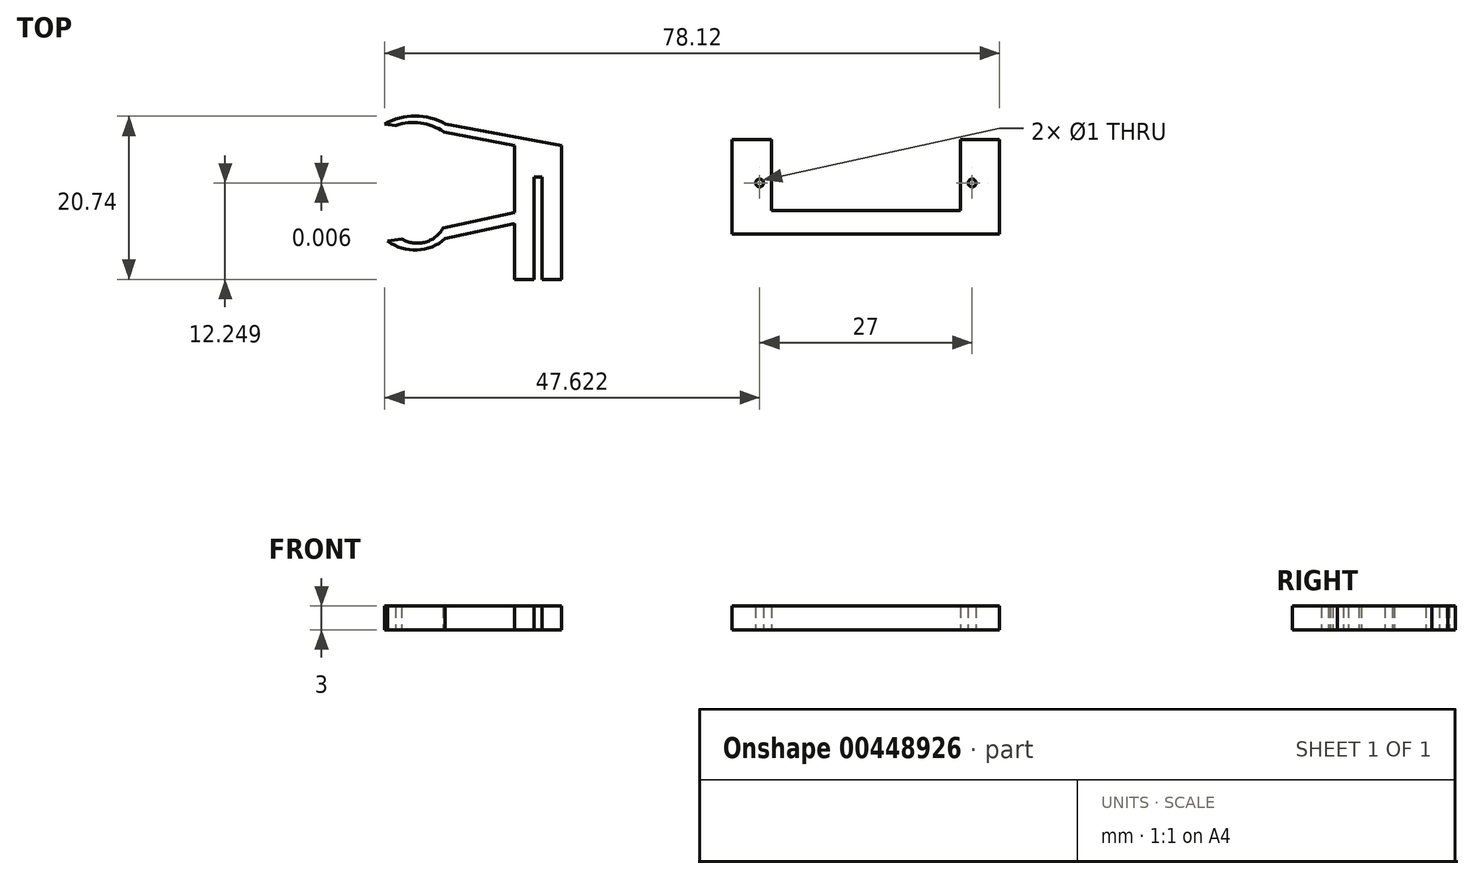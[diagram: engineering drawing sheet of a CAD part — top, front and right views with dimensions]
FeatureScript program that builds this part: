
annotation { "Feature Type Name" : "Feature", "Feature Type Description" : "" }
export const myFeature = defineFeature(function(context is Context, id is Id, definition is map)
    precondition{}
    {
        {
            var Q0;
            Q0=qCreatedBy(makeId("Top.planeOp"),FACE);
            var sketch = newSketch(context, id + "F0", { "sketchPlane" : qUnion([Q0])});
            skLineSegment(sketch, "E0.bottom", {"start": v(14.51, -20.17) * mm, "end": v(48.51, -20.17) * mm});
            skLineSegment(sketch, "E0.top", {"start": v(14.51, -23.17) * mm, "end": v(48.51, -23.17) * mm});
            skLineSegment(sketch, "E0.left", {"start": v(14.51, -20.17) * mm, "end": v(14.51, -23.17) * mm});
            skLineSegment(sketch, "E0.right", {"start": v(48.51, -20.17) * mm, "end": v(48.51, -23.17) * mm});
            skLineSegment(sketch, "E1.bottom", {"start": v(14.51, -23.17) * mm, "end": v(19.51, -23.17) * mm});
            skLineSegment(sketch, "E1.top", {"start": v(14.51, -11.17) * mm, "end": v(19.51, -11.17) * mm});
            skLineSegment(sketch, "E1.left", {"start": v(14.51, -23.17) * mm, "end": v(14.51, -11.17) * mm});
            skLineSegment(sketch, "E1.right", {"start": v(19.51, -23.17) * mm, "end": v(19.51, -11.17) * mm});
            skLineSegment(sketch, "E2.bottom", {"start": v(48.51, -23.17) * mm, "end": v(43.51, -23.17) * mm});
            skLineSegment(sketch, "E3", {"start": v(43.51, -23.17) * mm, "end": v(43.51, -11.18) * mm});
            skLineSegment(sketch, "E4", {"start": v(48.51, -23.17) * mm, "end": v(48.51, -11.17) * mm});
            skLineSegment(sketch, "E5", {"start": v(48.51, -11.17) * mm, "end": v(43.51, -11.18) * mm});
            skCircle(sketch, "E6", {"center": v(45.01, -16.68) * mm, "radius": 0.5 * mm});
            skCircle(sketch, "E7", {"center": v(18.01, -16.67) * mm, "radius": 0.5 * mm});
            skSolve(sketch);
        }
        {
            var Q0;
            {var subQ5=sQuery(id+"F0.wireOp",EDGE,"E1.bottom");Q0=makeQuery(id+"F0.imprint","IMPRINT",FACE,{"disambiguationData":[TD([[makeQuery(id+"F0.imprint","IMPRINT",EDGE,{"derivedFrom":subQ5}),1.0]])]});}
            var Q1;
            {var subQ1=sQuery(id+"F0.wireOp",EDGE,"E1.top");Q1=makeQuery(id+"F0.imprint","IMPRINT",FACE,{"disambiguationData":[TD([[makeQuery(id+"F0.imprint","IMPRINT",EDGE,{"derivedFrom":subQ1}),-1.0]])]});}
            var Q2;
            {var subQ5=sQuery(id+"F0.wireOp",EDGE,"E2.bottom");Q2=makeQuery(id+"F0.imprint","IMPRINT",FACE,{"disambiguationData":[TD([[makeQuery(id+"F0.imprint","IMPRINT",EDGE,{"derivedFrom":subQ5}),-1.0]])]});}
            var Q3;
            {var subQ0=sQuery(id+"F0.wireOp",EDGE,"E5");Q3=makeQuery(id+"F0.imprint","IMPRINT",FACE,{"disambiguationData":[TD([[makeQuery(id+"F0.imprint","IMPRINT",EDGE,{"derivedFrom":subQ0}),1.0]])]});}
            var Q4;
            {var subQ5=sQuery(id+"F0.wireOp",EDGE,"E0.top");Q4=makeQuery(id+"F0.imprint","IMPRINT",FACE,{"disambiguationData":[TD([[makeQuery(id+"F0.imprint","IMPRINT",EDGE,{"derivedFrom":subQ5}),1.0]])]});}
            extrude(context, id + "F1", {"entities" : qUnion([Q0, Q1, Q2, Q3, Q4]), "depth" : 3 * mm});
        }
        {
            var Q0;
            Q0=qCreatedBy(makeId("Top.planeOp"),FACE);
            var sketch = newSketch(context, id + "F2", { "sketchPlane" : qUnion([Q0])});
            skLineSegment(sketch, "E8.bottom", {"start": v(-13.12, -11.93) * mm, "end": v(-7.12, -11.93) * mm});
            skLineSegment(sketch, "E8.top", {"start": v(-13.12, -28.93) * mm, "end": v(-7.12, -28.93) * mm});
            skLineSegment(sketch, "E8.left", {"start": v(-13.12, -11.93) * mm, "end": v(-13.12, -28.93) * mm});
            skLineSegment(sketch, "E8.right", {"start": v(-7.12, -11.93) * mm, "end": v(-7.12, -28.93) * mm});
            skLineSegment(sketch, "E9.bottom", {"start": v(-10.62, -15.93) * mm, "end": v(-9.62, -15.93) * mm});
            skLineSegment(sketch, "E9.top", {"start": v(-10.62, -28.93) * mm, "end": v(-9.62, -28.93) * mm});
            skLineSegment(sketch, "E9.left", {"start": v(-10.62, -15.93) * mm, "end": v(-10.62, -28.93) * mm});
            skLineSegment(sketch, "E9.right", {"start": v(-9.62, -15.93) * mm, "end": v(-9.62, -28.93) * mm});
            skLineSegment(sketch, "E10.bottom", {"start": v(-13.12, -27.9) * mm, "end": v(-12.42, -27.9) * mm});
            skLineSegment(sketch, "E10.top", {"start": v(-13.12, -24.9) * mm, "end": v(-12.42, -24.9) * mm});
            skLineSegment(sketch, "E10.left", {"start": v(-13.12, -27.9) * mm, "end": v(-13.12, -24.9) * mm});
            skLineSegment(sketch, "E10.right", {"start": v(-12.42, -27.9) * mm, "end": v(-12.42, -24.9) * mm});
            skLineSegment(sketch, "E11.bottom", {"start": v(-7.12, -27.9) * mm, "end": v(-7.82, -27.9) * mm});
            skLineSegment(sketch, "E11.top", {"start": v(-7.12, -24.9) * mm, "end": v(-7.82, -24.9) * mm});
            skLineSegment(sketch, "E11.left", {"start": v(-7.12, -27.9) * mm, "end": v(-7.12, -24.9) * mm});
            skLineSegment(sketch, "E11.right", {"start": v(-7.82, -27.9) * mm, "end": v(-7.82, -24.9) * mm});
            skLineSegment(sketch, "E12", {"start": v(-13.12, -21.81) * mm, "end": v(-21.91, -23.74) * mm});
            skLineSegment(sketch, "E13", {"start": v(-13.12, -20.43) * mm, "end": v(-22.2, -22.42) * mm});
            skLineSegment(sketch, "E14", {"start": v(-22.2, -22.42) * mm, "end": v(-21.91, -23.74) * mm});
            skArc(sketch, "E15", {"start": v(-27.44, -23.8) * mm, "mid": v(-24.53, -24.21) * mm, "end": v(-22.2, -22.42) * mm});
            skArc(sketch, "E16", {"start": v(-29.22, -24.07) * mm, "mid": v(-25.5, -25.2) * mm, "end": v(-21.91, -23.74) * mm});
            skLineSegment(sketch, "E17", {"start": v(-27.44, -23.8) * mm, "end": v(-29.22, -24.07) * mm});
            skLineSegment(sketch, "E18", {"start": v(-7.12, -11.93) * mm, "end": v(-21.87, -9.17) * mm});
            skLineSegment(sketch, "E19", {"start": v(-13.12, -11.93) * mm, "end": v(-22.08, -10.2) * mm});
            skLineSegment(sketch, "E20", {"start": v(-22.08, -10.2) * mm, "end": v(-21.87, -9.17) * mm});
            skArc(sketch, "E21", {"start": v(-21.87, -9.17) * mm, "mid": v(-25.74, -8.19) * mm, "end": v(-29.61, -9.17) * mm});
            skLineSegment(sketch, "E22", {"start": v(-29.61, -9.17) * mm, "end": v(-28.2, -9.36) * mm});
            skPoint(sketch, "E22.endSnap0", {"position": v(-29.11, -9.36) * mm});
            skArc(sketch, "E23", {"start": v(-22.08, -10.2) * mm, "mid": v(-25.04, -9.06) * mm, "end": v(-28.2, -9.36) * mm});
            skSolve(sketch);
        }
        {
            var Q0;
            Q0=makeQuery(id+"F2.imprint","IMPRINT",FACE,{"disambiguationData":[TD([[makeQuery(id+"F2.imprint","IMPRINT",EDGE,{"derivedFrom":sQuery(id+"F2.wireOp",EDGE,"E10.bottom")}),1.0]])]});
            var Q1;
            Q1=makeQuery(id+"F2.imprint","IMPRINT",FACE,{"disambiguationData":[TD([[makeQuery(id+"F2.imprint","IMPRINT",EDGE,{"derivedFrom":sQuery(id+"F2.wireOp",EDGE,"E11.bottom")}),-1.0]])]});
            var Q2;
            Q2=makeQuery(id+"F2.imprint","IMPRINT",FACE,{"disambiguationData":[TD([[makeQuery(id+"F2.imprint","IMPRINT",EDGE,{"derivedFrom":sQuery(id+"F2.wireOp",EDGE,"E14")}),-1.0]])]});
            var Q3;
            Q3=makeQuery(id+"F2.imprint","IMPRINT",FACE,{"disambiguationData":[TD([[makeQuery(id+"F2.imprint","IMPRINT",EDGE,{"derivedFrom":sQuery(id+"F2.wireOp",EDGE,"E20")}),1.0]])]});
            var Q4;
            Q4=makeQuery(id+"F2.imprint","IMPRINT",FACE,{"disambiguationData":[TD([[makeQuery(id+"F2.imprint","IMPRINT",EDGE,{"derivedFrom":sQuery(id+"F2.wireOp",EDGE,"E8.bottom")}),1.0]])]});
            var Q5;
            {var subQ0=sQuery(id+"F2.wireOp",EDGE,"E12");Q5=makeQuery(id+"F2.imprint","IMPRINT",FACE,{"disambiguationData":[TD([[makeQuery(id+"F2.imprint","IMPRINT",EDGE,{"derivedFrom":subQ0}),-1.0]])]});}
            var Q6;
            {var subQ5=sQuery(id+"F2.wireOp",EDGE,"E8.bottom");Q6=makeQuery(id+"F2.imprint","IMPRINT",FACE,{"disambiguationData":[TD([[makeQuery(id+"F2.imprint","IMPRINT",EDGE,{"derivedFrom":subQ5}),-1.0]])]});}
            extrude(context, id + "F3", {"entities" : qUnion([Q0, Q1, Q2, Q3, Q4, Q5, Q6]), "depth" : 3 * mm});
        }
    });
